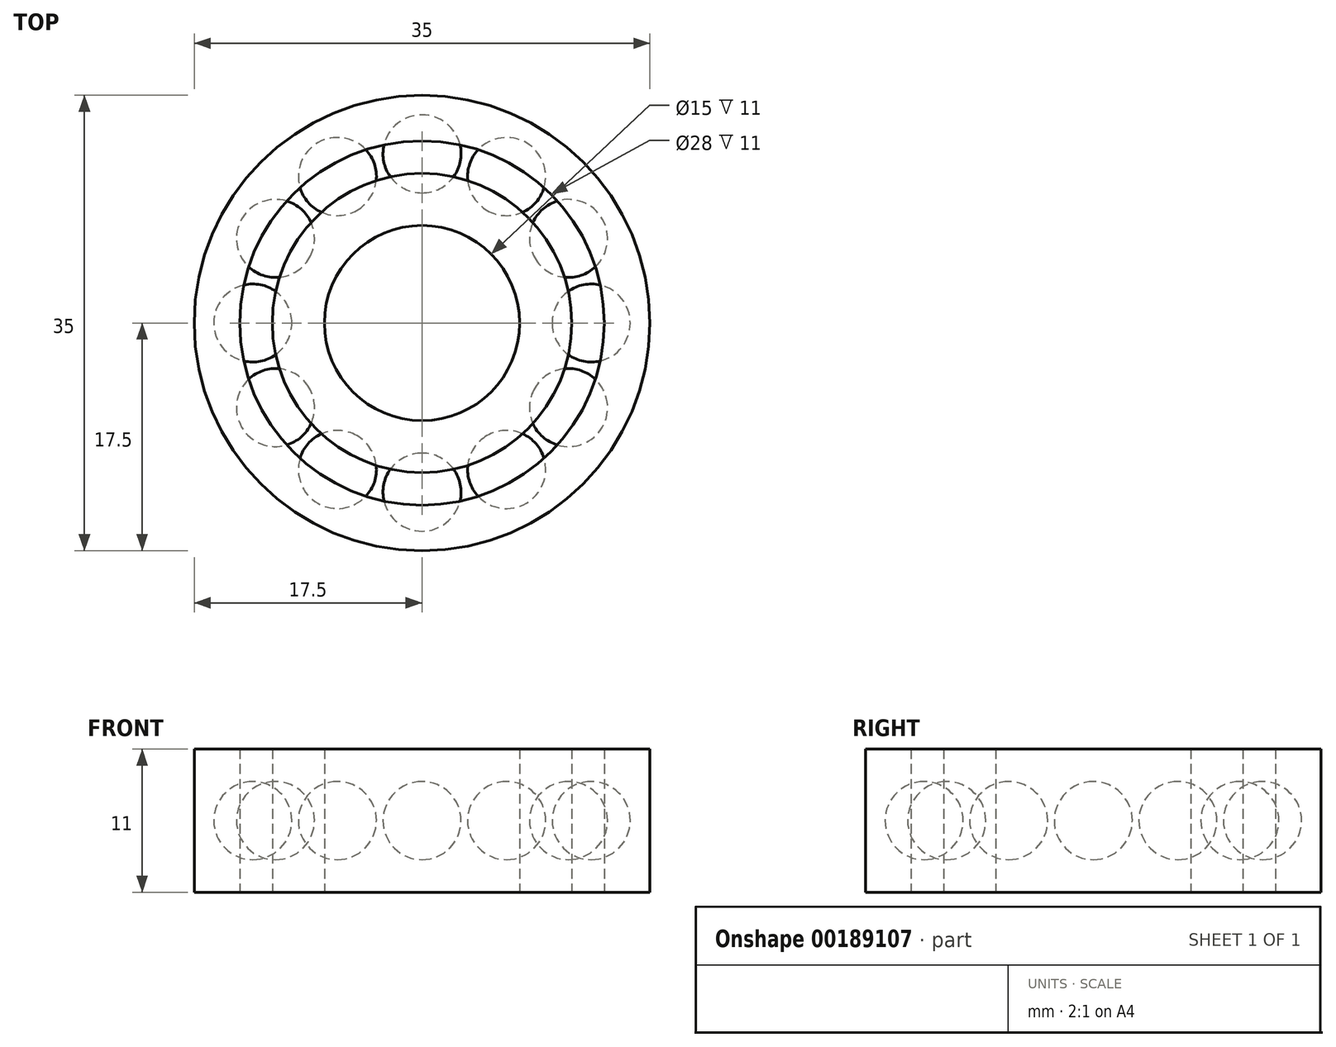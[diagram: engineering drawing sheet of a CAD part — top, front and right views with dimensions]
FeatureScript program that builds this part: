
annotation { "Feature Type Name" : "Feature", "Feature Type Description" : "" }
export const myFeature = defineFeature(function(context is Context, id is Id, definition is map)
    precondition{}
    {
        {
            var Q0;
            Q0=qCreatedBy(makeId("Top.planeOp"),FACE);
            var sketch = newSketch(context, id + "F0", { "sketchPlane" : qUnion([Q0])});
            skCircle(sketch, "E0", {"center": v(0, 0) * mm, "radius": 17.5 * mm});
            skCircle(sketch, "E1", {"center": v(0, 0) * mm, "radius": 14 * mm});
            skSolve(sketch);
        }
        {
            var Q0;
            Q0 = qSketchRegion(id + "F0", true);
            extrude(context, id + "F1", {"entities" : qUnion([Q0]), "depth" : 11 * mm});
        }
        {
            var Q0;
            Q0=qCreatedBy(makeId("Top.planeOp"),FACE);
            var sketch = newSketch(context, id + "F2", { "sketchPlane" : qUnion([Q0])});
            skCircle(sketch, "E2", {"center": v(0, 0) * mm, "radius": 7.5 * mm});
            skCircle(sketch, "E3", {"center": v(0, 0) * mm, "radius": 11.5 * mm});
            skSolve(sketch);
        }
        {
            var Q0;
            Q0 = qSketchRegion(id + "F2", true);
            extrude(context, id + "F3", {"entities" : qUnion([Q0]), "depth" : 11 * mm});
        }
        {
            var Q0;
            Q0=qCreatedBy(makeId("Right.planeOp"),FACE);
            var sketch = newSketch(context, id + "F4", { "sketchPlane" : qUnion([Q0])});
            skArc(sketch, "E4", {"start": v(-13, 8.5) * mm, "mid": v(-16, 5.5) * mm, "end": v(-13, 2.5) * mm});
            skLineSegment(sketch, "E5", {"start": v(-13, 8.5) * mm, "end": v(-13, 2.5) * mm});
            skSolve(sketch);
        }
        {
            var Q0;
            Q0 = qSketchRegion(id + "F4", true);
            var Q1;
            Q1=sQuery(id+"F4.wireOp",EDGE,"E5");
            revolve(context, id + "F5", {"entities" : qUnion([Q0]), "axis" : qUnion([Q1]), "revolveType" : RevolveType.FULL});
        }
        {
            var Q0;
            Q0=makeQuery(id+"F5.opRevolve","SWEPT_BODY",BODY,{"disambiguationData":[OSD([sQuery(id+"F4.wireOp",EDGE,"E4"),sQuery(id+"F4.wireOp",EDGE,"E5")])]});
            var Q1;
            Q1=makeQuery(id+"F3.opExtrude","CAP_EDGE",EDGE,{"disambiguationData":[OSD([sQuery(id+"F2.wireOp",EDGE,"E3")])],"isStart":false});
            circularPattern(context, id + "F6", {"entities" : qUnion([Q0]), "axis" : qUnion([Q1]), "angle" : 30 * degree, "instanceCount" : 12});
        }
    });
